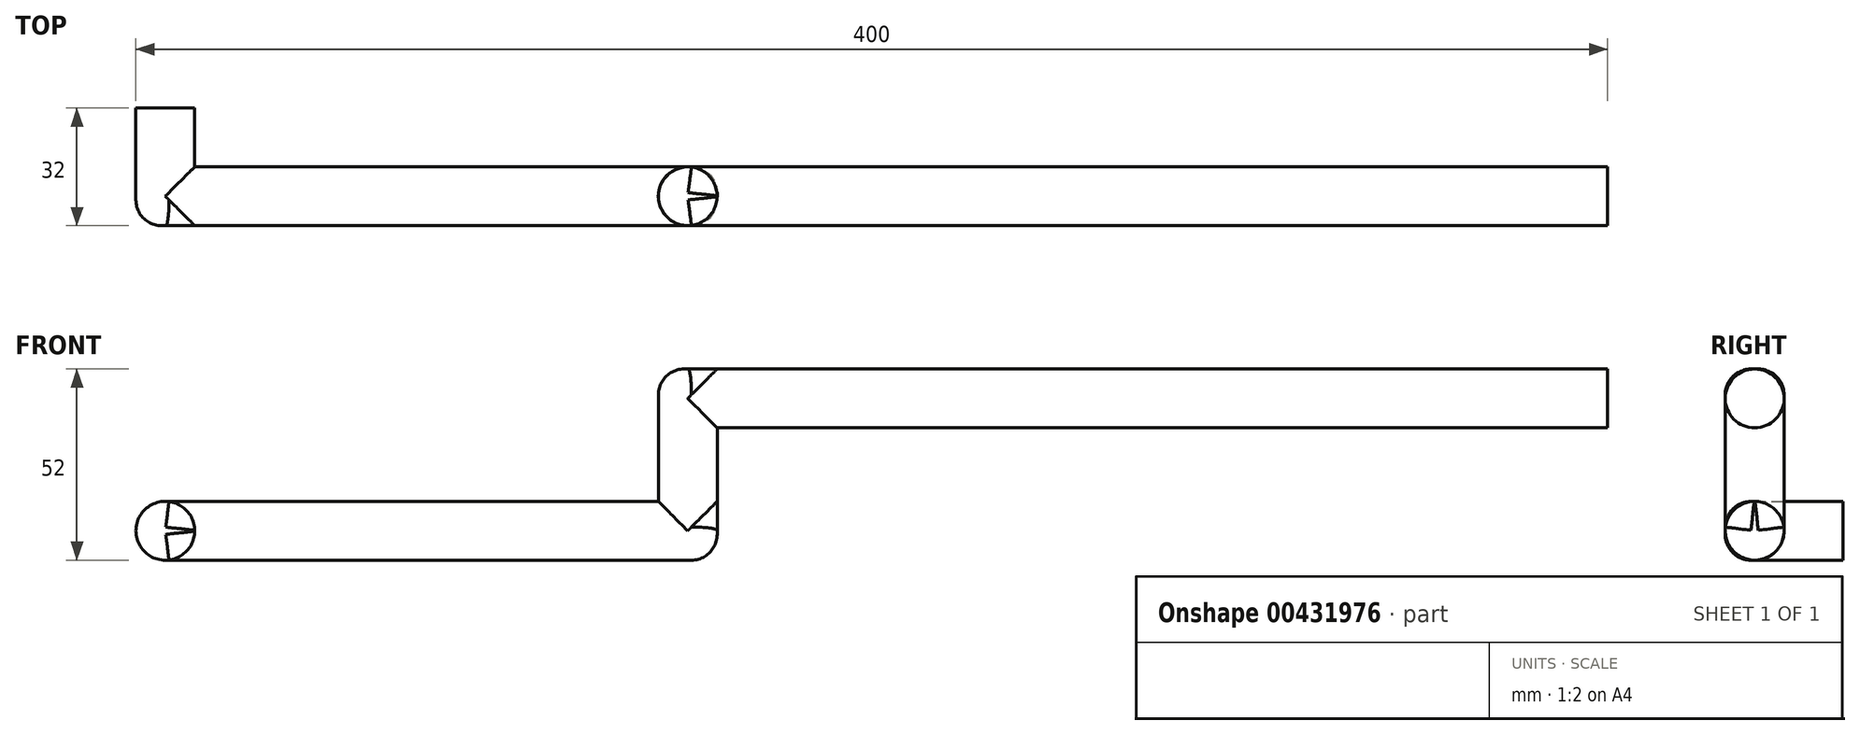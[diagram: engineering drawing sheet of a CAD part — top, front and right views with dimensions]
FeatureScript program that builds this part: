
annotation { "Feature Type Name" : "Feature", "Feature Type Description" : "" }
export const myFeature = defineFeature(function(context is Context, id is Id, definition is map)
    precondition{}
    {
        {
            var Q0;
            Q0=qCreatedBy(makeId("Front.planeOp"),FACE);
            var sketch = newSketch(context, id + "F0", { "sketchPlane" : qUnion([Q0])});
            skCircle(sketch, "E0", {"center": v(0, 0) * mm, "radius": 8 * mm});
            skSolve(sketch);
        }
        {
            var Q0;
            Q0=qSketchRegion(id+"F0",true);
            extrude(context, id + "F1", {"entities" : qUnion([Q0]), "depth" : 32 * mm, "offsetDistance" : 25 * mm});
        }
        {
            var Q0;
            Q0=qCreatedBy(makeId("Right.planeOp"),FACE);
            var sketch = newSketch(context, id + "F2", { "sketchPlane" : qUnion([Q0])});
            skCircle(sketch, "E1", {"center": v(-24, 0) * mm, "radius": 8 * mm});
            skSolve(sketch);
        }
        {
            var Q0;
            Q0=qSketchRegion(id+"F2",true);
            extrude(context, id + "F3", {"entities" : qUnion([Q0]), "operationType" : NewBodyOperationType.ADD, "depth" : 150 * mm});
        }
        {
            var Q0;
            Q0=makeQuery(id+"F1.opExtrude","CAP_EDGE",EDGE,{"disambiguationData":[OSD([sQuery(id+"F0.wireOp",EDGE,"E0")])],"isStart":false});
            fillet(context, id + "F4", {"entities" : qUnion([Q0]), "radius" : 7 * mm, "tangentPropagation" : true, "allowEdgeOverflow" : false});
        }
        {
            var Q0;
            Q0=qCreatedBy(makeId("Top.planeOp"),FACE);
            var sketch = newSketch(context, id + "F5", { "sketchPlane" : qUnion([Q0])});
            skCircle(sketch, "E2", {"center": v(142, -24) * mm, "radius": 8 * mm});
            skLineSegment(sketch, "E3.0", {"start": v(150, -16) * mm, "end": v(150, -32) * mm, "construction": true});
            skPoint(sketch, "E4", {"position": v(150, -24) * mm});
            skLineSegment(sketch, "E5", {"start": v(150, -24) * mm, "end": v(143.44, -24) * mm, "construction": true});
            skSolve(sketch);
        }
        {
            var Q0;
            Q0=qSketchRegion(id+"F5",true);
            extrude(context, id + "F6", {"entities" : qUnion([Q0]), "operationType" : NewBodyOperationType.ADD, "depth" : 44 * mm});
        }
        {
            var Q0;
            Q0=qCreatedBy(makeId("Right.planeOp"),FACE);
            cPlane(context, id + "F7", {"entities" : qUnion([Q0]), "cplaneType" : CPlaneType.OFFSET, "offset" : 142 * mm, "width" : 150 * mm, "height" : 150 * mm});
        }
        {
            var Q0;
            Q0=qCreatedBy(id+"F7.planeOp",FACE);
            var sketch = newSketch(context, id + "F8", { "sketchPlane" : qUnion([Q0])});
            skCircle(sketch, "E6", {"center": v(-24, 36) * mm, "radius": 8 * mm});
            skLineSegment(sketch, "E7.0", {"start": v(-32, 44) * mm, "end": v(-16, 44) * mm, "construction": true});
            skLineSegment(sketch, "E8", {"start": v(-24, 44) * mm, "end": v(-24, 36) * mm, "construction": true});
            skSolve(sketch);
        }
        {
            var Q0;
            Q0=qSketchRegion(id+"F8",true);
            extrude(context, id + "F9", {"entities" : qUnion([Q0]), "operationType" : NewBodyOperationType.ADD, "depth" : 250 * mm});
        }
        {
            var Q0;
            Q0=makeQuery(id+"F6.opExtrude","CAP_EDGE",EDGE,{"disambiguationData":[OSD([sQuery(id+"F5.wireOp",EDGE,"E2")])],"isStart":false});
            var Q1;
            Q1=makeQuery(id+"F3.opExtrude","CAP_EDGE",EDGE,{"disambiguationData":[OSD([sQuery(id+"F2.wireOp",EDGE,"E1")])],"isStart":false});
            fillet(context, id + "F10", {"entities" : qUnion([Q0, Q1]), "radius" : 7 * mm, "tangentPropagation" : true, "allowEdgeOverflow" : false});
        }
    });
